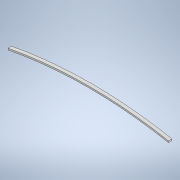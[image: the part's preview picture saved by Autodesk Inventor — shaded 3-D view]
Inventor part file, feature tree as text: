
AUTODESK INVENTOR PART (.ipt)
format: ipt  version: 2020.2 (Build 242310000, 310)  size: 103,424 bytes
history: native  units: mm
features: extrude x1, sketch x1
ambient origin geometry x8: Origin, YZ Plane, XZ Plane, XY Plane, X Axis, Y Axis, Z Axis, Center Point
bodies: Solide1 (feature_tree)
feature tree (2):
  extrude  "Extrusion1"  Depth=785.7mm
  sketch  "Esquisse1"
